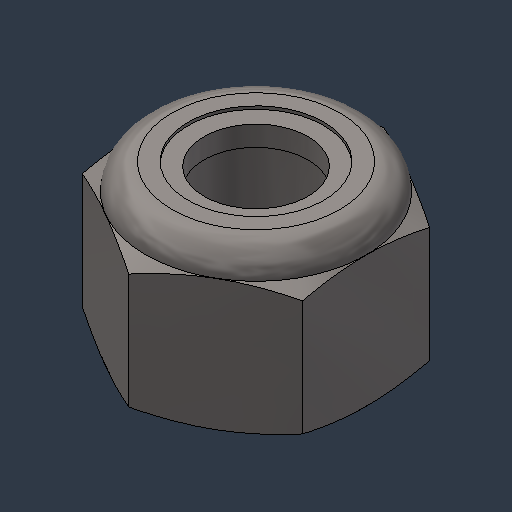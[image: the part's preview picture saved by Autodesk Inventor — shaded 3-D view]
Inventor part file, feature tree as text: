
AUTODESK INVENTOR PART (.ipt)
format: ipt  version: 2024.3 (Build 283343000, 343)  size: 176,128 bytes
history: native  units: mm (DEFAULTED — no unit token found)
features: other x1, revolve x1
ambient origin geometry x8: Origin, YZ Plane, XZ Plane, XY Plane, X Axis, Y Axis, Z Axis, Center Point
bodies: Solid1 (feature_tree), Solid2 (feature_tree)
feature tree (2):
  other  "Cut-Revolve2"
  revolve  "Revolve1"  [1 undecoded]
note: 1 required parameter value undecoded (feature->parameter linkage not recoverable at this tier; creation-order binding heuristic only, values carry confidence <= 0.55)
